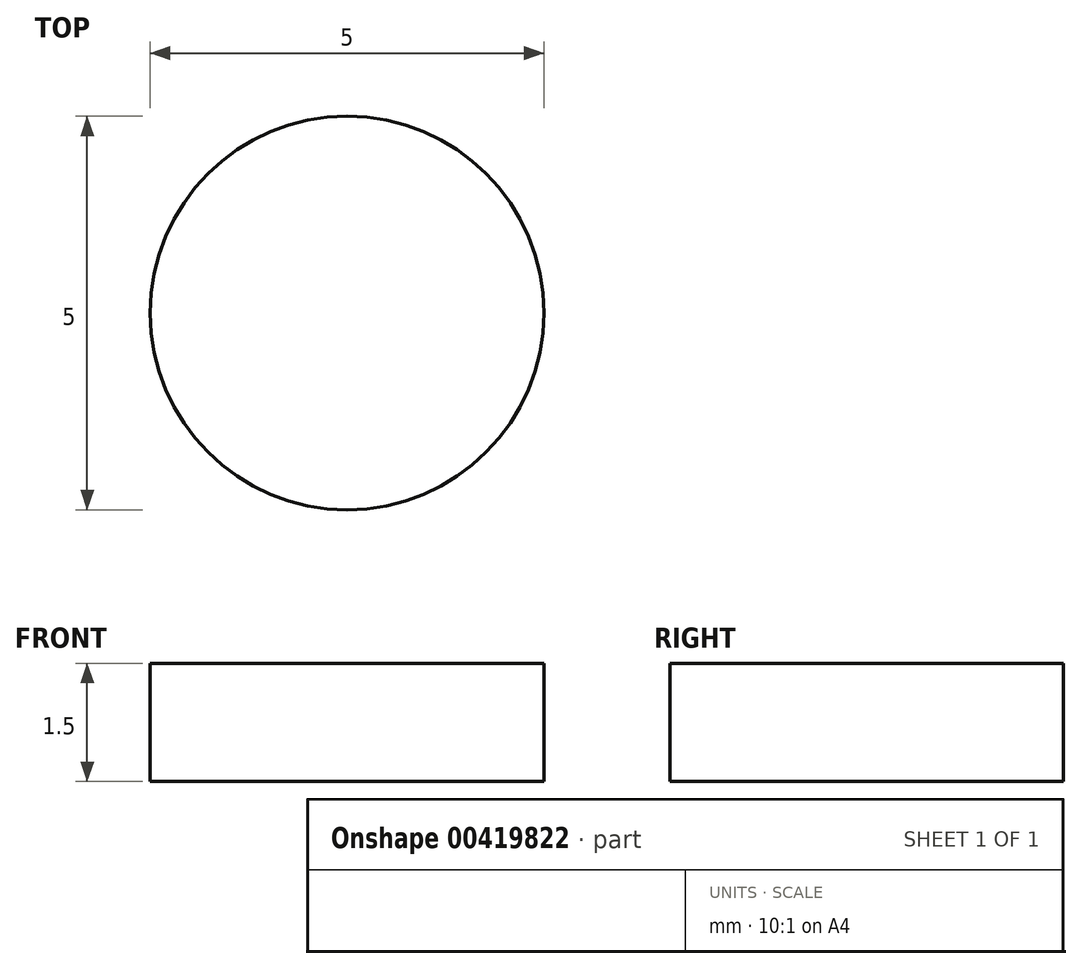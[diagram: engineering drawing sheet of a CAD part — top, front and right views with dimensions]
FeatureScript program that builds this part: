
annotation { "Feature Type Name" : "Feature", "Feature Type Description" : "" }
export const myFeature = defineFeature(function(context is Context, id is Id, definition is map)
    precondition{}
    {
        {
            var Q0;
            Q0=qCreatedBy(makeId("Top.planeOp"),FACE);
            var sketch = newSketch(context, id + "F0", { "sketchPlane" : qUnion([Q0])});
            skCircle(sketch, "E0", {"center": v(0, 0) * mm, "radius": 9 * mm});
            skSolve(sketch);
        }
        {
            var Q0;
            Q0=sQuery(id+"F0.wireOp",EDGE,"E0");
            extrude(context, id + "F1", {"bodyType" : ToolBodyType.SURFACE, "flatOperationType" : FlatOperationType.REMOVE, "surfaceEntities" : qUnion([Q0]), "oppositeDirection" : true, "offsetDistance" : 25 * mm, "depth" : (65 - 1.5) * mm, "domain" : OperationDomain.MODEL});
        }
        {
            var Q0;
            Q0=qCreatedBy(makeId("Top.planeOp"), FACE);
            var sketch = newSketch(context, id + "F2", { "sketchPlane" : qUnion([Q0])});
            skCircle(sketch, "E1", {"center": v(0, 0) * mm, "radius": 2.5 * mm});
            skSolve(sketch);
        }
        {
            var Q0;
            Q0 = qSketchRegion(id + "F2", true);
            extrude(context, id + "F3", {"entities" : qUnion([Q0]), "domain" : OperationDomain.MODEL, "flatOperationType" : FlatOperationType.REMOVE, "depth" : 1.5 * mm, "offsetDistance" : 25 * mm});
        }
    });
